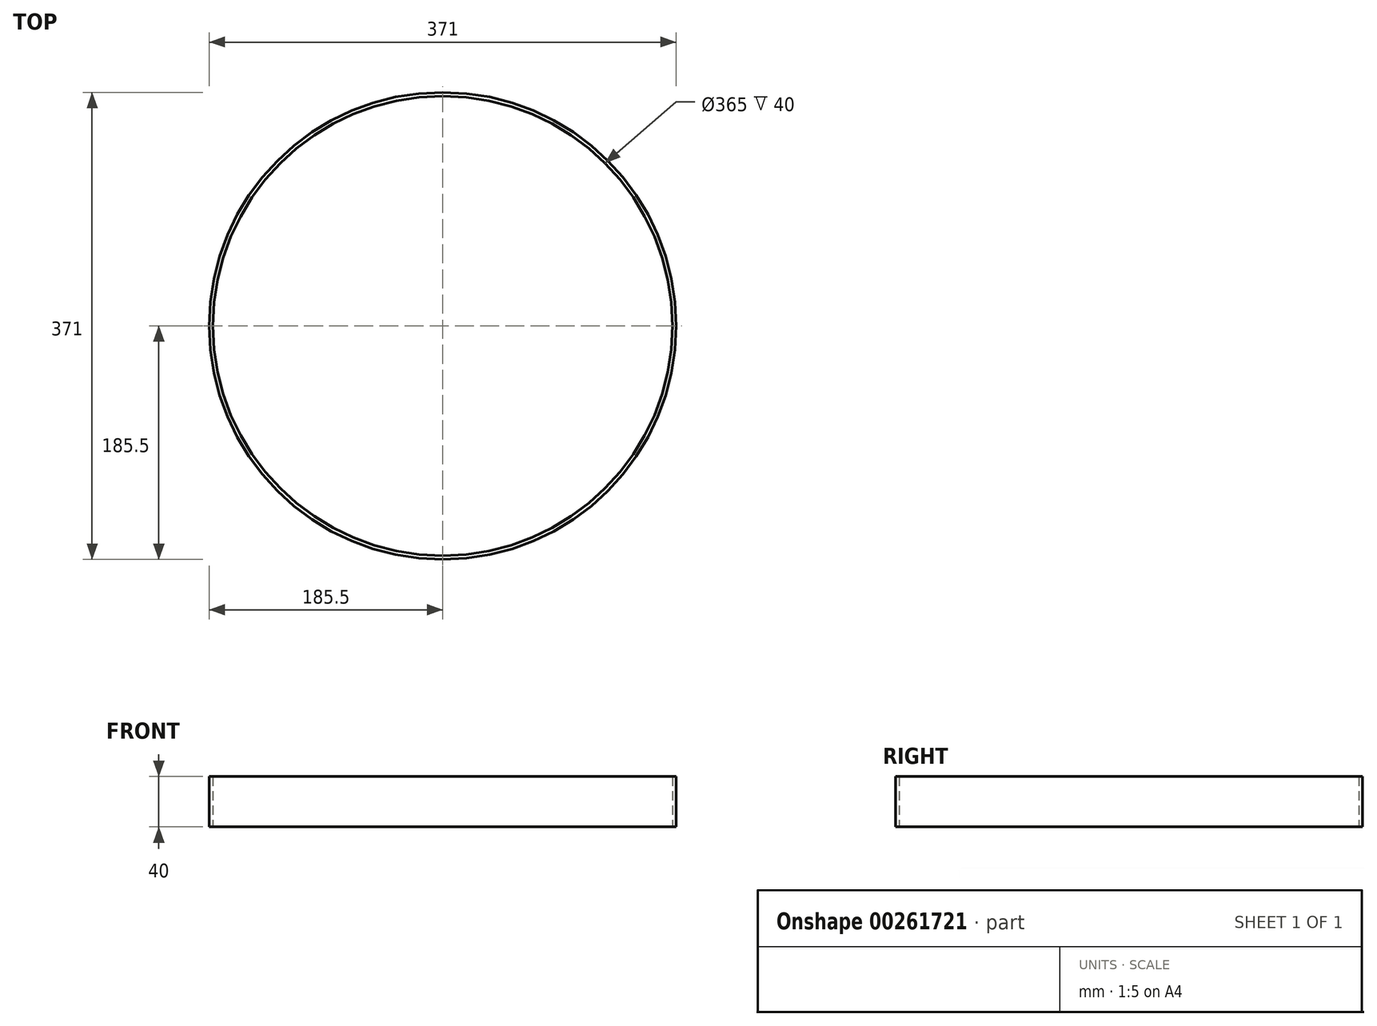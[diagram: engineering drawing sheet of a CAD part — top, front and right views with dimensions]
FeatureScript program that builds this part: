
annotation { "Feature Type Name" : "Feature", "Feature Type Description" : "" }
export const myFeature = defineFeature(function(context is Context, id is Id, definition is map)
    precondition{}
    {
        {
            var Q0;
            Q0=qCreatedBy(makeId("Top.planeOp"),FACE);
            var sketch = newSketch(context, id + "F0", { "sketchPlane" : qUnion([Q0])});
            skCircle(sketch, "E0", {"center": v(0, 0) * mm, "radius": 185.5 * mm});
            skCircle(sketch, "E1", {"center": v(0, 0) * mm, "radius": 182.5 * mm});
            skSolve(sketch);
        }
        {
            var Q0;
            Q0 = qSketchRegion(id + "F0", true);
            extrude(context, id + "F1", {"entities" : qUnion([Q0]), "depth" : 40 * mm});
        }
    });
